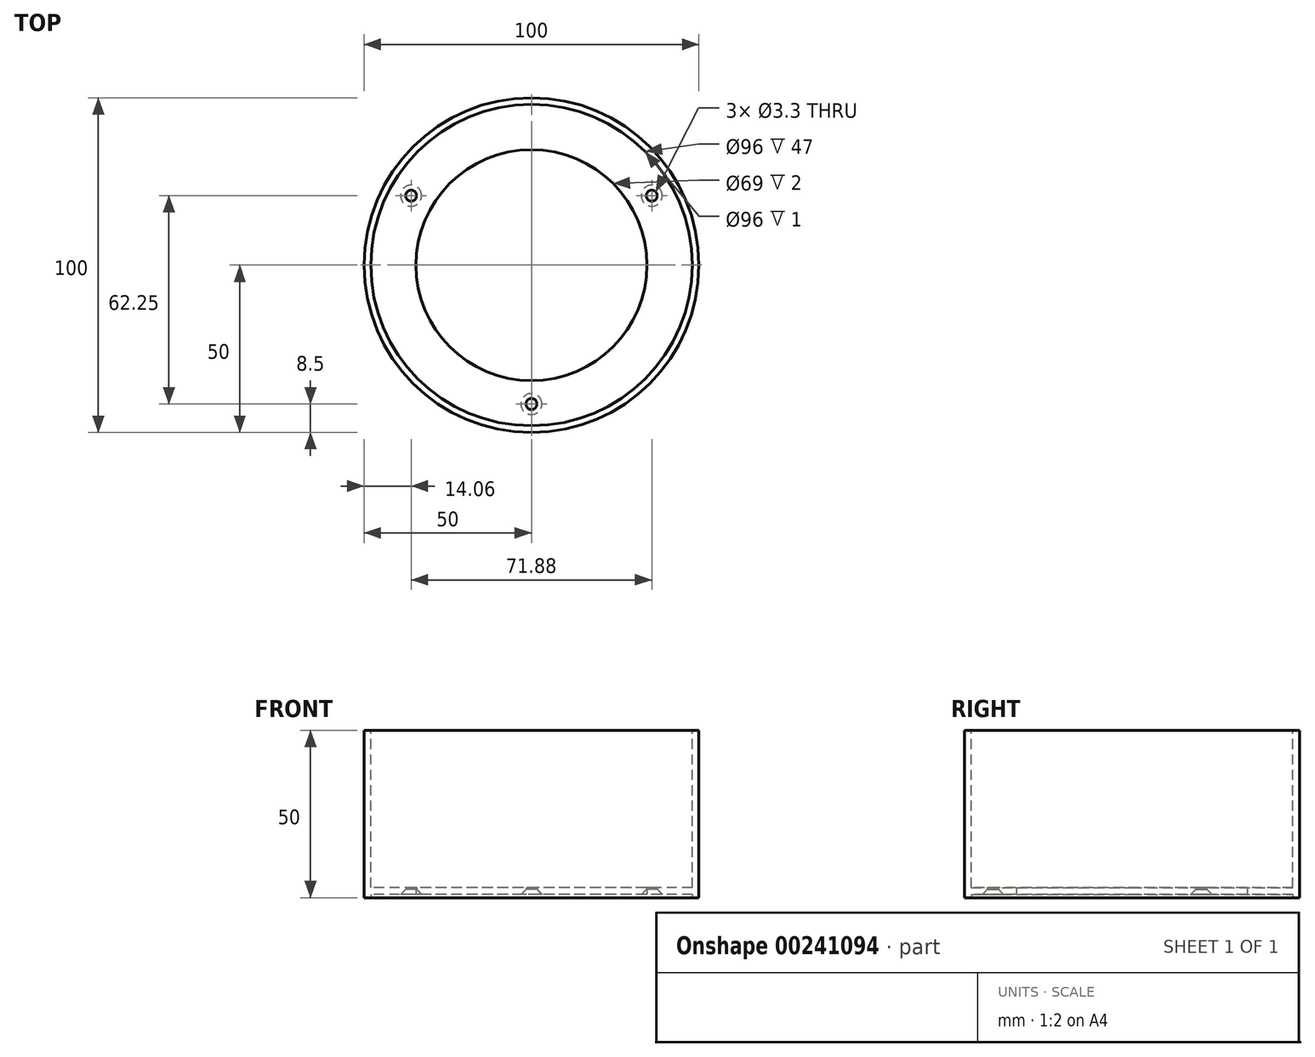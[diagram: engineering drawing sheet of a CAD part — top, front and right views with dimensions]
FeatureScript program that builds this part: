
annotation { "Feature Type Name" : "Feature", "Feature Type Description" : "" }
export const myFeature = defineFeature(function(context is Context, id is Id, definition is map)
    precondition{}
    {
        {
            var Q0;
            Q0=qCreatedBy(makeId("Top.planeOp"),FACE);
            var sketch = newSketch(context, id + "F0", { "sketchPlane" : qUnion([Q0])});
            skCircle(sketch, "E0", {"center": v(0, 0) * mm, "radius": 50 * mm});
            skSolve(sketch);
        }
        {
            var Q0;
            Q0=qCreatedBy(makeId("Top.planeOp"),FACE);
            cPlane(context, id + "F1", {"entities" : qUnion([Q0]), "cplaneType" : CPlaneType.OFFSET, "offset" : 50 * mm, "width" : 150 * mm, "height" : 150 * mm});
        }
        {
            var Q0;
            Q0=qCreatedBy(id+"F1.planeOp",FACE);
            var sketch = newSketch(context, id + "F2", { "sketchPlane" : qUnion([Q0])});
            skCircle(sketch, "E1", {"center": v(0, 0) * mm, "radius": 48 * mm});
            skSolve(sketch);
        }
        {
            var Q0;
            Q0=makeQuery(id+"F0.imprint","IMPRINT",FACE,{"disambiguationData":[TD([[makeQuery(id+"F0.imprint","IMPRINT",EDGE,{"derivedFrom":sQuery(id+"F0.wireOp",EDGE,"E0")}),1.0]])]});
            extrude(context, id + "F3", {"entities" : qUnion([Q0]), "depth" : 50 * mm});
        }
        {
            var Q0;
            Q0=makeQuery(id+"F2.imprint","IMPRINT",FACE,{"disambiguationData":[TD([[makeQuery(id+"F2.imprint","IMPRINT",EDGE,{"derivedFrom":sQuery(id+"F2.wireOp",EDGE,"E1")}),1.0]])]});
            extrude(context, id + "F4", {"entities" : qUnion([Q0]), "operationType" : NewBodyOperationType.REMOVE, "oppositeDirection" : true, "depth" : 47 * mm});
        }
        {
            var Q0;
            Q0=qCreatedBy(makeId("Top.planeOp"),FACE);
            var sketch = newSketch(context, id + "F5", { "sketchPlane" : qUnion([Q0])});
            skCircle(sketch, "E2", {"center": v(0, 0) * mm, "radius": 34.5 * mm});
            skSolve(sketch);
        }
        {
            var Q0;
            Q0 = qSketchRegion(id + "F5", true);
            extrude(context, id + "F6", {"entities" : qUnion([Q0]), "operationType" : NewBodyOperationType.REMOVE, "depth" : 3 * mm});
        }
        {
            var Q0;
            Q0=qCreatedBy(makeId("Top.planeOp"),FACE);
            var sketch = newSketch(context, id + "F7", { "sketchPlane" : qUnion([Q0])});
            skCircle(sketch, "E3", {"center": v(0, 0) * mm, "radius": 48 * mm});
            skSolve(sketch);
        }
        {
            var Q0;
            Q0 = qSketchRegion(id + "F7", true);
            extrude(context, id + "F8", {"entities" : qUnion([Q0]), "operationType" : NewBodyOperationType.REMOVE, "depth" : 1 * mm});
        }
        {
            var Q0;
            Q0=qCreatedBy(makeId("Top.planeOp"),FACE);
            var sketch = newSketch(context, id + "F9", { "sketchPlane" : qUnion([Q0])});
            skCircle(sketch, "E4", {"center": v(0, -41.5) * mm, "radius": 1.65 * mm});
            skCircle(sketch, "E5.1.0", {"center": v(35.94, 20.75) * mm, "radius": 1.65 * mm});
            skCircle(sketch, "E5.2.0", {"center": v(-35.94, 20.75) * mm, "radius": 1.65 * mm});
            skPoint(sketch, "E5.center", {"position": v(0, 0) * mm});
            skSolve(sketch);
        }
        {
            var Q0;
            Q0 = qSketchRegion(id + "F9", true);
            extrude(context, id + "F10", {"entities" : qUnion([Q0]), "operationType" : NewBodyOperationType.REMOVE, "depth" : 25 * mm});
        }
        {
            var Q0;
            Q0=qCreatedBy(makeId("Top.planeOp"),FACE);
            cPlane(context, id + "F11", {"entities" : qUnion([Q0]), "cplaneType" : CPlaneType.OFFSET, "offset" : 1 * mm, "width" : 150 * mm, "height" : 150 * mm});
        }
        {
            var Q0;
            Q0=makeQuery(id+"F10.boolean.opBoolean","INTERSECT",EDGE,{"derivedFrom":[makeQuery(id+"F8.boolean.opBoolean","COPY",FACE,{"derivedFrom":makeQuery(id+"F8.opExtrude","CAP_FACE",FACE,{"disambiguationData":[OSD([sQuery(id+"F7.wireOp",EDGE,"E3")])],"isStart":false})}),makeQuery(id+"F10.opExtrude","SWEPT_FACE",FACE,{"disambiguationData":[OSD([sQuery(id+"F9.wireOp",EDGE,"E5.2.0")])]})]});
            var Q1;
            Q1=makeQuery(id+"F10.boolean.opBoolean","INTERSECT",EDGE,{"derivedFrom":[makeQuery(id+"F8.boolean.opBoolean","COPY",FACE,{"derivedFrom":makeQuery(id+"F8.opExtrude","CAP_FACE",FACE,{"disambiguationData":[OSD([sQuery(id+"F7.wireOp",EDGE,"E3")])],"isStart":false})}),makeQuery(id+"F10.opExtrude","SWEPT_FACE",FACE,{"disambiguationData":[OSD([sQuery(id+"F9.wireOp",EDGE,"E4")])]})]});
            var Q2;
            Q2=makeQuery(id+"F10.boolean.opBoolean","INTERSECT",EDGE,{"derivedFrom":[makeQuery(id+"F8.boolean.opBoolean","COPY",FACE,{"derivedFrom":makeQuery(id+"F8.opExtrude","CAP_FACE",FACE,{"disambiguationData":[OSD([sQuery(id+"F7.wireOp",EDGE,"E3")])],"isStart":false})}),makeQuery(id+"F10.opExtrude","SWEPT_FACE",FACE,{"disambiguationData":[OSD([sQuery(id+"F9.wireOp",EDGE,"E5.1.0")])]})]});
            chamfer(context, id + "F12", {"entities" : qUnion([Q0, Q1, Q2]), "width" : 1.5 * mm, "tangentPropagation" : true});
        }
    });
